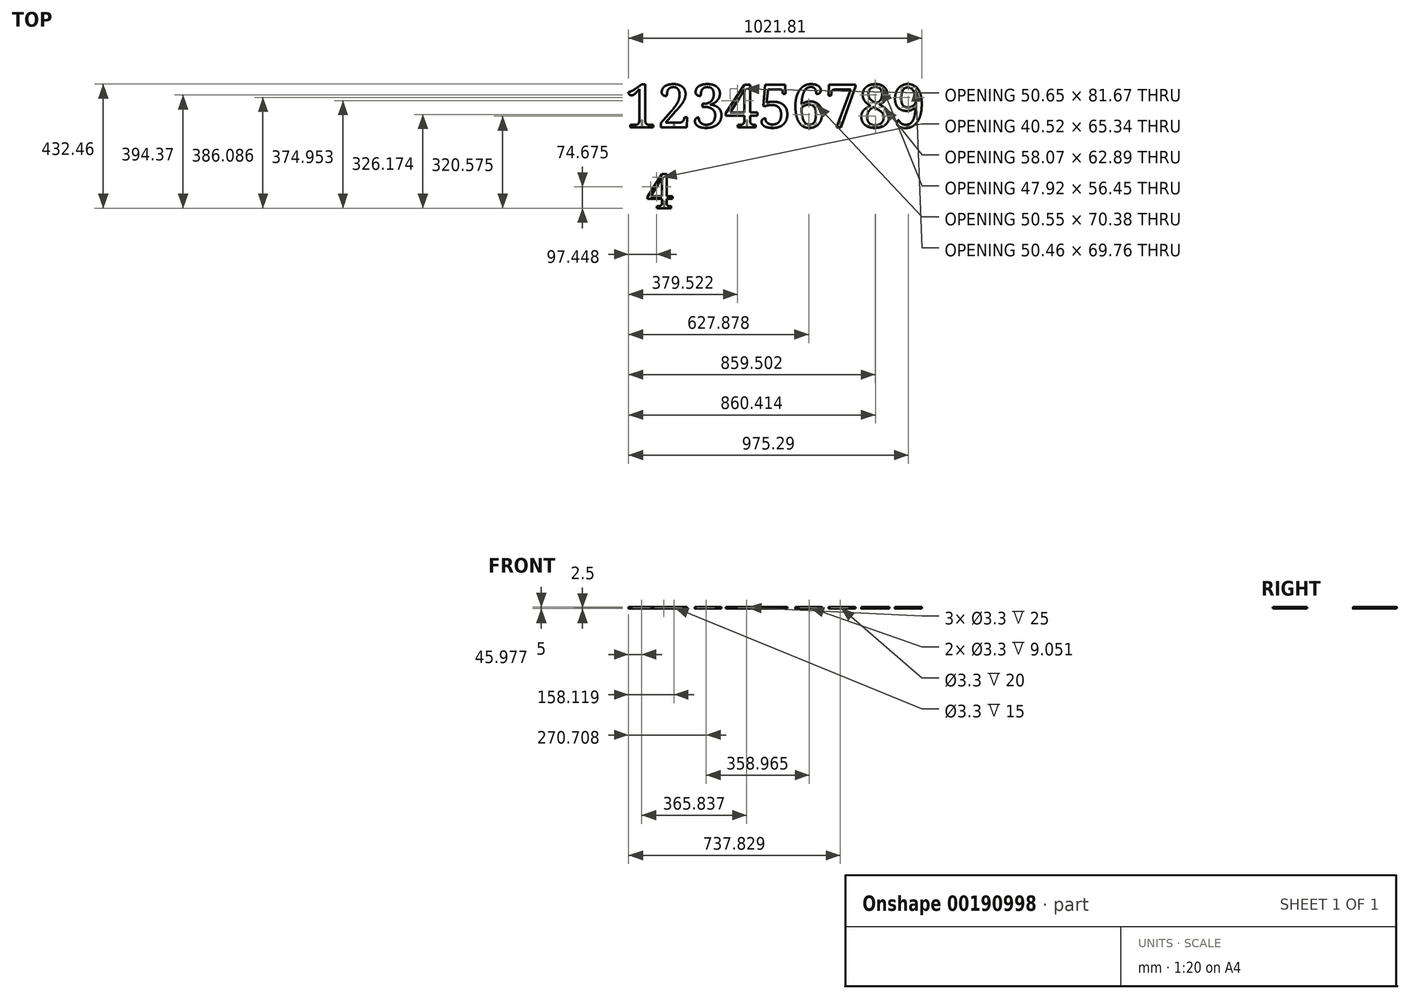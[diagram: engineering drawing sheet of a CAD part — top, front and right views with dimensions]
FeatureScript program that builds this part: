
annotation { "Feature Type Name" : "Feature", "Feature Type Description" : "" }
export const myFeature = defineFeature(function(context is Context, id is Id, definition is map)
    precondition{}
    {
        {
            var Q0;
            Q0=qCreatedBy(makeId("Top.planeOp"),FACE);
            var sketch = newSketch(context, id + "F0", { "sketchPlane" : qUnion([Q0])});
            skText(sketch, "E0", { "text": "123456789", "fontName": "NotoSerif-Regular.ttf"});
            const initialGuessF0  = {"E0": [0, 0, 1, 0, 0.15]};
            skSetInitialGuess(sketch, initialGuessF0);
            skSolve(sketch);
        }
        {
            var Q0;
            Q0 = qSketchRegion(id + "F0", true);
            extrude(context, id + "F1", {"entities" : qUnion([Q0]), "depth" : 5 * mm});
        }
        {
            var Q0;
            Q0=makeQuery(id+"F1.opExtrude","SWEPT_FACE",FACE,{"disambiguationData":[OSD([sQuery(id+"F0.wireOp",EDGE,"E0.sketch_text.stroke-26")])]});
            var sketch = newSketch(context, id + "F2", { "sketchPlane" : qUnion([Q0])});
            skCircle(sketch, "E1", {"center": v(59.72, 2.5) * mm, "radius": 1.65 * mm});
            skPoint(sketch, "E1.centerSnap0", {"position": v(20.05, 2.5) * mm});
            skPoint(sketch, "E1.centerSnap1", {"position": v(59.72, 0) * mm});
            skSolve(sketch);
        }
        {
            var Q0;
            Q0 = qSketchRegion(id + "F2", true);
            extrude(context, id + "F3", {"entities" : qUnion([Q0]), "operationType" : NewBodyOperationType.REMOVE, "oppositeDirection" : true, "depth" : 25 * mm});
        }
        {
            var Q0;
            Q0=makeQuery(id+"F1.opExtrude","SWEPT_FACE",FACE,{"disambiguationData":[OSD([sQuery(id+"F0.wireOp",EDGE,"E0.sketch_text.stroke-40")])]});
            var sketch = newSketch(context, id + "F4", { "sketchPlane" : qUnion([Q0])});
            skCircle(sketch, "E2", {"center": v(171.86, 2.5) * mm, "radius": 1.65 * mm});
            skPoint(sketch, "E2.centerSnap0", {"position": v(171.86, 0) * mm});
            skPoint(sketch, "E2.centerSnap1", {"position": v(127.05, 2.5) * mm});
            skSolve(sketch);
        }
        {
            var Q0;
            Q0 = qSketchRegion(id + "F4", true);
            extrude(context, id + "F5", {"entities" : qUnion([Q0]), "operationType" : NewBodyOperationType.REMOVE, "oppositeDirection" : true, "depth" : 15 * mm});
        }
        {
            var Q0;
            Q0=qCreatedBy(makeId("Front.planeOp"),FACE);
            var sketch = newSketch(context, id + "F6", { "sketchPlane" : qUnion([Q0])});
            skCircle(sketch, "E3", {"center": v(284.45, 2.5) * mm, "radius": 1.65 * mm});
            skSolve(sketch);
        }
        {
            var Q0;
            Q0 = qSketchRegion(id + "F6", true);
            extrude(context, id + "F7", {"entities" : qUnion([Q0]), "operationType" : NewBodyOperationType.REMOVE, "oppositeDirection" : true, "depth" : 7 * mm, "hasSecondDirection" : true, "secondDirectionOppositeDirection" : false, "secondDirectionDepth" : 15 * mm});
        }
        {
            var Q0;
            Q0=makeQuery(id+"F1.opExtrude","SWEPT_FACE",FACE,{"disambiguationData":[OSD([sQuery(id+"F0.wireOp",EDGE,"E0.sketch_text.stroke-135")])]});
            var sketch = newSketch(context, id + "F8", { "sketchPlane" : qUnion([Q0])});
            skCircle(sketch, "E4", {"center": v(425.55, 2.5) * mm, "radius": 1.65 * mm});
            skPoint(sketch, "E4.centerSnap0", {"position": v(425.55, 0) * mm});
            skPoint(sketch, "E4.centerSnap1", {"position": v(394.17, 2.5) * mm});
            skSolve(sketch);
        }
        {
            var Q0;
            Q0 = qSketchRegion(id + "F8", true);
            extrude(context, id + "F9", {"entities" : qUnion([Q0]), "operationType" : NewBodyOperationType.REMOVE, "oppositeDirection" : true, "depth" : 25 * mm});
        }
        {
            var Q0;
            Q0=qCreatedBy(makeId("Front.planeOp"),FACE);
            var sketch = newSketch(context, id + "F10", { "sketchPlane" : qUnion([Q0])});
            skCircle(sketch, "E5", {"center": v(513.53, 2.5) * mm, "radius": 1.65 * mm});
            skSolve(sketch);
        }
        {
            var Q0;
            Q0 = qSketchRegion(id + "F10", true);
            extrude(context, id + "F11", {"entities" : qUnion([Q0]), "operationType" : NewBodyOperationType.REMOVE, "oppositeDirection" : true, "depth" : 8 * mm, "hasSecondDirection" : true, "secondDirectionOppositeDirection" : false, "secondDirectionDepth" : 25 * mm});
        }
        {
            var Q0;
            Q0=qCreatedBy(makeId("Front.planeOp"),FACE);
            var sketch = newSketch(context, id + "F12", { "sketchPlane" : qUnion([Q0])});
            skCircle(sketch, "E6", {"center": v(643.41, 2.5) * mm, "radius": 1.65 * mm});
            skSolve(sketch);
        }
        {
            var Q0;
            Q0 = qSketchRegion(id + "F12", true);
            extrude(context, id + "F13", {"entities" : qUnion([Q0]), "operationType" : NewBodyOperationType.REMOVE, "oppositeDirection" : true, "depth" : 7 * mm, "hasSecondDirection" : true, "secondDirectionOppositeDirection" : false, "secondDirectionDepth" : 25 * mm});
        }
        {
            var Q0;
            Q0=makeQuery(id+"F1.opExtrude","SWEPT_FACE",FACE,{"disambiguationData":[OSD([sQuery(id+"F0.wireOp",EDGE,"E0.sketch_text.stroke-263")])]});
            var sketch = newSketch(context, id + "F14", { "sketchPlane" : qUnion([Q0])});
            skCircle(sketch, "E7", {"center": v(751.57, 2.5) * mm, "radius": 1.65 * mm});
            skPoint(sketch, "E7.centerSnap0", {"position": v(754.07, 2.5) * mm});
            skSolve(sketch);
        }
        {
            var Q0;
            Q0 = qSketchRegion(id + "F14", true);
            extrude(context, id + "F15", {"entities" : qUnion([Q0]), "operationType" : NewBodyOperationType.REMOVE, "oppositeDirection" : true, "depth" : 20 * mm});
        }
        {
            var Q0;
            Q0=qCreatedBy(makeId("Front.planeOp"),FACE);
            var sketch = newSketch(context, id + "F16", { "sketchPlane" : qUnion([Q0])});
            skCircle(sketch, "E8", {"center": v(871.58, 2.5) * mm, "radius": 1.65 * mm});
            skSolve(sketch);
        }
        {
            var Q0;
            Q0 = qSketchRegion(id + "F16", true);
            extrude(context, id + "F17", {"entities" : qUnion([Q0]), "operationType" : NewBodyOperationType.REMOVE, "oppositeDirection" : true, "depth" : 5 * mm, "hasSecondDirection" : true, "secondDirectionOppositeDirection" : false, "secondDirectionDepth" : 25 * mm});
        }
        {
            var Q0;
            Q0=qCreatedBy(makeId("Front.planeOp"),FACE);
            var sketch = newSketch(context, id + "F18", { "sketchPlane" : qUnion([Q0])});
            skCircle(sketch, "E9", {"center": v(987.35, 2.5) * mm, "radius": 1.65 * mm});
            skSolve(sketch);
        }
        {
            var Q0;
            Q0 = qSketchRegion(id + "F18", true);
            extrude(context, id + "F19", {"entities" : qUnion([Q0]), "operationType" : NewBodyOperationType.REMOVE, "oppositeDirection" : true, "depth" : 7 * mm, "hasSecondDirection" : true, "secondDirectionOppositeDirection" : false, "secondDirectionDepth" : 25 * mm});
        }
        {
            var Q0;
            Q0=qCreatedBy(makeId("Top.planeOp"),FACE);
            var sketch = newSketch(context, id + "F20", { "sketchPlane" : qUnion([Q0])});
            skText(sketch, "E10", { "text": "4", "fontName": "NotoSerif-Regular.ttf"});
            const initialGuessF20  = {"E10": [0.07611, -0.28161, 1, 0, 0.12]};
            skSetInitialGuess(sketch, initialGuessF20);
            skSolve(sketch);
        }
        {
            var Q0;
            Q0 = qSketchRegion(id + "F20", true);
            extrude(context, id + "F21", {"entities" : qUnion([Q0]), "depth" : 5 * mm});
        }
        {
            var Q0;
            Q0=makeQuery(id+"F21.opExtrude","SWEPT_FACE",FACE,{"disambiguationData":[OSD([sQuery(id+"F20.wireOp",EDGE,"E10.sketch_text.stroke-7")])]});
            var sketch = newSketch(context, id + "F22", { "sketchPlane" : qUnion([Q0])});
            skCircle(sketch, "E11", {"center": v(137.02, 2.5) * mm, "radius": 1.65 * mm});
            skPoint(sketch, "E11.centerSnap0", {"position": v(137.02, 5) * mm});
            skPoint(sketch, "E11.centerSnap1", {"position": v(111.92, 2.5) * mm});
            skSolve(sketch);
        }
        {
            var Q0;
            Q0 = qSketchRegion(id + "F22", true);
            extrude(context, id + "F23", {"entities" : qUnion([Q0]), "operationType" : NewBodyOperationType.REMOVE, "oppositeDirection" : true, "depth" : 25 * mm});
        }
    });
